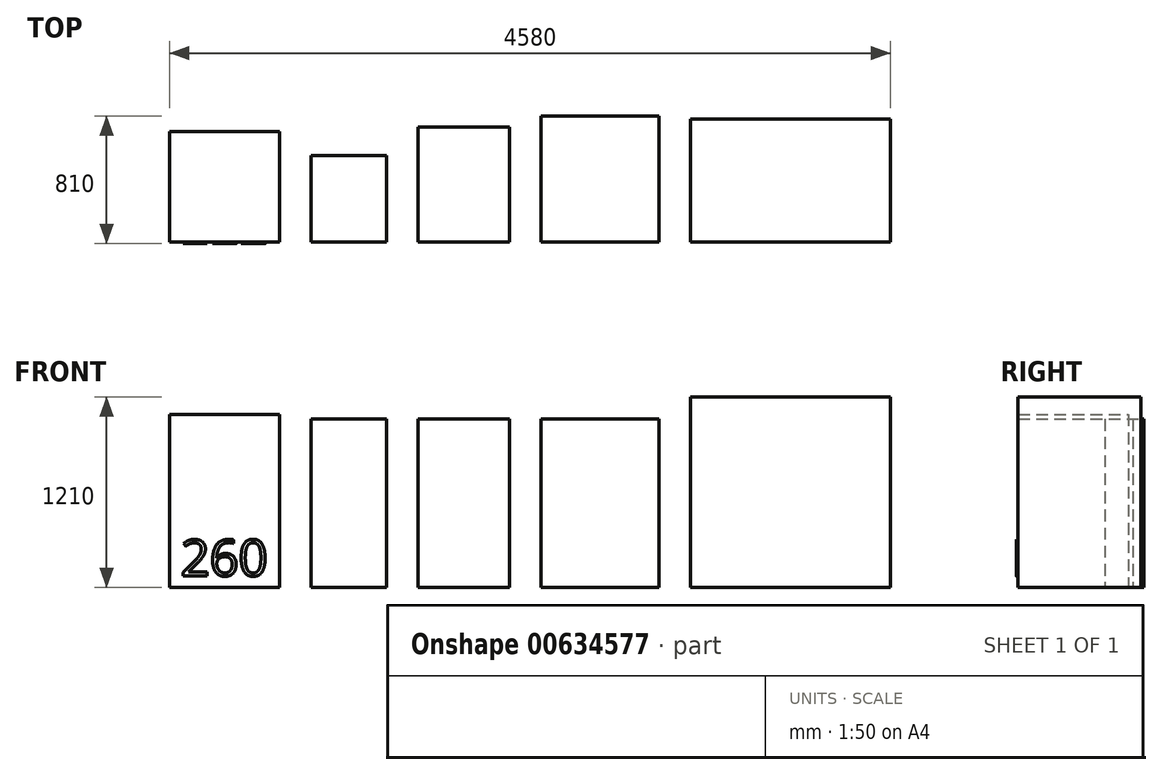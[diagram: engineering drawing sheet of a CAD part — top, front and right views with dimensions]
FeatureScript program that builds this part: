
annotation { "Feature Type Name" : "Feature", "Feature Type Description" : "" }
export const myFeature = defineFeature(function(context is Context, id is Id, definition is map)
    precondition{}
    {
        {
            var Q0;
            Q0=qCreatedBy(makeId("Top.planeOp"),FACE);
            var sketch = newSketch(context, id + "F0", { "sketchPlane" : qUnion([Q0])});
            skLineSegment(sketch, "E0.bottom", {"start": v(0, 0) * mm, "end": v(700, 0) * mm});
            skLineSegment(sketch, "E0.top", {"start": v(0, 700) * mm, "end": v(700, 700) * mm});
            skLineSegment(sketch, "E0.left", {"start": v(0, 0) * mm, "end": v(0, 700) * mm});
            skLineSegment(sketch, "E0.right", {"start": v(700, 0) * mm, "end": v(700, 700) * mm});
            skLineSegment(sketch, "E1.bottom", {"start": v(900, 0) * mm, "end": v(1380, 0) * mm});
            skLineSegment(sketch, "E1.top", {"start": v(900, 550) * mm, "end": v(1380, 550) * mm});
            skLineSegment(sketch, "E1.left", {"start": v(900, 0) * mm, "end": v(900, 550) * mm});
            skLineSegment(sketch, "E1.right", {"start": v(1380, 0) * mm, "end": v(1380, 550) * mm});
            skLineSegment(sketch, "E2.bottom", {"start": v(1580, 0) * mm, "end": v(2160, 0) * mm});
            skLineSegment(sketch, "E2.top", {"start": v(1580, 730) * mm, "end": v(2160, 730) * mm});
            skLineSegment(sketch, "E2.left", {"start": v(1580, 0) * mm, "end": v(1580, 730) * mm});
            skLineSegment(sketch, "E2.right", {"start": v(2160, 0) * mm, "end": v(2160, 730) * mm});
            skLineSegment(sketch, "E3.bottom", {"start": v(2360, 0) * mm, "end": v(3110, 0) * mm});
            skLineSegment(sketch, "E3.top", {"start": v(2360, 800) * mm, "end": v(3110, 800) * mm});
            skLineSegment(sketch, "E3.left", {"start": v(2360, 0) * mm, "end": v(2360, 800) * mm});
            skLineSegment(sketch, "E3.right", {"start": v(3110, 0) * mm, "end": v(3110, 800) * mm});
            skLineSegment(sketch, "E4.bottom", {"start": v(3310, 0) * mm, "end": v(4580, 0) * mm});
            skLineSegment(sketch, "E4.top", {"start": v(3310, 780) * mm, "end": v(4580, 780) * mm});
            skLineSegment(sketch, "E4.left", {"start": v(3310, 0) * mm, "end": v(3310, 780) * mm});
            skLineSegment(sketch, "E4.right", {"start": v(4580, 0) * mm, "end": v(4580, 780) * mm});
            skSolve(sketch);
        }
        {
            var Q0;
            Q0=makeQuery(id+"F0.imprint","IMPRINT",FACE,{"disambiguationData":[TD([[makeQuery(id+"F0.imprint","IMPRINT",EDGE,{"derivedFrom":sQuery(id+"F0.wireOp",EDGE,"E0.bottom")}),1.0]])]});
            extrude(context, id + "F1", {"entities" : qUnion([Q0]), "depth" : 1100 * mm, "offsetDistance" : 25 * mm});
        }
        {
            var Q0;
            Q0=makeQuery(id+"F0.imprint","IMPRINT",FACE,{"disambiguationData":[TD([[makeQuery(id+"F0.imprint","IMPRINT",EDGE,{"derivedFrom":sQuery(id+"F0.wireOp",EDGE,"E1.bottom")}),1.0]])]});
            extrude(context, id + "F2", {"entities" : qUnion([Q0]), "depth" : 1070 * mm, "offsetDistance" : 25 * mm});
        }
        {
            var Q0;
            Q0=makeQuery(id+"F0.imprint","IMPRINT",FACE,{"disambiguationData":[TD([[makeQuery(id+"F0.imprint","IMPRINT",EDGE,{"derivedFrom":sQuery(id+"F0.wireOp",EDGE,"E2.bottom")}),1.0]])]});
            var Q1;
            Q1=makeQuery(id+"F0.imprint","IMPRINT",FACE,{"disambiguationData":[TD([[makeQuery(id+"F0.imprint","IMPRINT",EDGE,{"derivedFrom":sQuery(id+"F0.wireOp",EDGE,"E3.bottom")}),1.0]])]});
            extrude(context, id + "F3", {"entities" : qUnion([Q0, Q1]), "depth" : 1070 * mm, "offsetDistance" : 25 * mm});
        }
        {
            var Q0;
            Q0=makeQuery(id+"F0.imprint","IMPRINT",FACE,{"disambiguationData":[TD([[makeQuery(id+"F0.imprint","IMPRINT",EDGE,{"derivedFrom":sQuery(id+"F0.wireOp",EDGE,"E4.bottom")}),1.0]])]});
            extrude(context, id + "F4", {"entities" : qUnion([Q0]), "depth" : 1210 * mm, "offsetDistance" : 25 * mm});
        }
        {
            var Q0;
            Q0=makeQuery(id+"F1.opExtrude","SWEPT_FACE",FACE,{"disambiguationData":[OSD([sQuery(id+"F0.wireOp",EDGE,"E0.bottom")])]});
            var sketch = newSketch(context, id + "F5", { "sketchPlane" : qUnion([Q0])});
            skText(sketch, "E5", { "text": "260", "fontName": "OpenSans-Regular.ttf"});
            const initialGuessF5  = {"E5": [0.0712, 0.07333, 1, 0, 0.23168]};
            skSetInitialGuess(sketch, initialGuessF5);
            skSolve(sketch);
        }
        {
            var Q0;
            Q0 = qSketchRegion(id + "F5", true);
            extrude(context, id + "F6", {"entities" : qUnion([Q0]), "operationType" : NewBodyOperationType.ADD, "depth" : 10 * mm, "offsetDistance" : 25 * mm});
        }
    });
